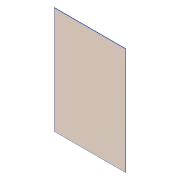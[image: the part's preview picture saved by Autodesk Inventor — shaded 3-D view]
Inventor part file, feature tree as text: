
AUTODESK INVENTOR PART (.ipt)
format: ipt  version: 2016 (Build 200138000, 138)  size: 181,760 bytes
history: native  units: in
note: dims shown in document units (in); Inventor stores cm internally (conversion verified against a paired STEP export)
features: sheet_metal_op x7, other x6, reference x6, sketch x5, fillet x1
ambient origin geometry x8: Origin, YZ Plane, XZ Plane, XY Plane, X Axis, Y Axis, Z Axis, Center Point
bodies: Solid1 (feature_tree)
feature tree (25):
  sheet_metal_op  "Face1"
  sheet_metal_op  "Flange1"
  sketch  "Sketch5"  dims[d8=3.0in]
  sheet_metal_op  "Flange2"
  fillet  "Fillet1"  Radius=30.0in
  sketch  "Sketch1"  dims[d1=30.0in]
  other  "Plate1"
  sketch  "Sketch3"  dims[d2=0.125in]
  reference  "Reference12"
  reference  "Reference13"
  reference  "Reference14"
  sketch  "Sketch4"  dims[d7=60.0deg]
  other  "Plate2"
  sheet_metal_op  "Bend1"
  sheet_metal_op  "Corner1"
  reference  "Reference15"
  reference  "Reference16"
  reference  "Reference17"
  sketch  "Sketch6"  dims[d9=180.0deg d10=90.0deg d11=13.0167in d12=0.125in d13=0.0in d14=0.125in d15=0.0625in d16=0.25in d17=0.125in d18=5.0in d19=90.0deg d20=0.125in d21=0.5in d22=0.125in d23=0.125in d24=0.125in d25=0.0625in d26=0.25in d27=0.125in d28=5.0in d29=90.0deg d30=0.125in d31=0.5in d32=0.125in d33=0.125in d36=1.063in d37=0.125in d38=0.0in d39=0.125in]
  other  "Plate3"
  sheet_metal_op  "Bend2"
  sheet_metal_op  "Corner2"
  other  "Cut1"
  other  "Cut2"
  other  "Definition1"
